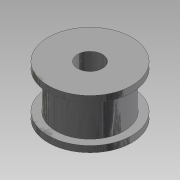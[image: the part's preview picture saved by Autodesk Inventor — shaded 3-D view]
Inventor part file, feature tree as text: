
AUTODESK INVENTOR PART (.ipt)
format: ipt  version: 2014 (Build 180170000, 170)  size: 104,448 bytes
history: native  units: mm
features: extrude x4, sketch x4
ambient origin geometry x8: Origin, YZ Plane, XZ Plane, XY Plane, X Axis, Y Axis, Z Axis, Center Point
bodies: Solid1 (feature_tree)
feature tree (8):
  extrude  "Extrusion1"  Depth=1.0mm TaperAngle=0.0deg
  extrude  "Extrusion2"  Depth=6.0mm TaperAngle=0.0deg
  extrude  "Extrusion3"  Depth=1.0mm TaperAngle=0.0deg
  extrude  "Extrusion4"  Depth=15.0mm TaperAngle=0.0deg
  sketch  "Sketch1"  dims[d0=13.5mm d1=1.0mm d2=0.0mm]
  sketch  "Sketch2"  dims[d3=11.0mm d4=6.0mm d5=0.0mm]
  sketch  "Sketch3"  dims[d6=13.5mm d7=1.0mm d8=0.0mm]
  sketch  "Sketch4"  dims[d9=4.0mm d10=15.0mm d11=0.0mm]
